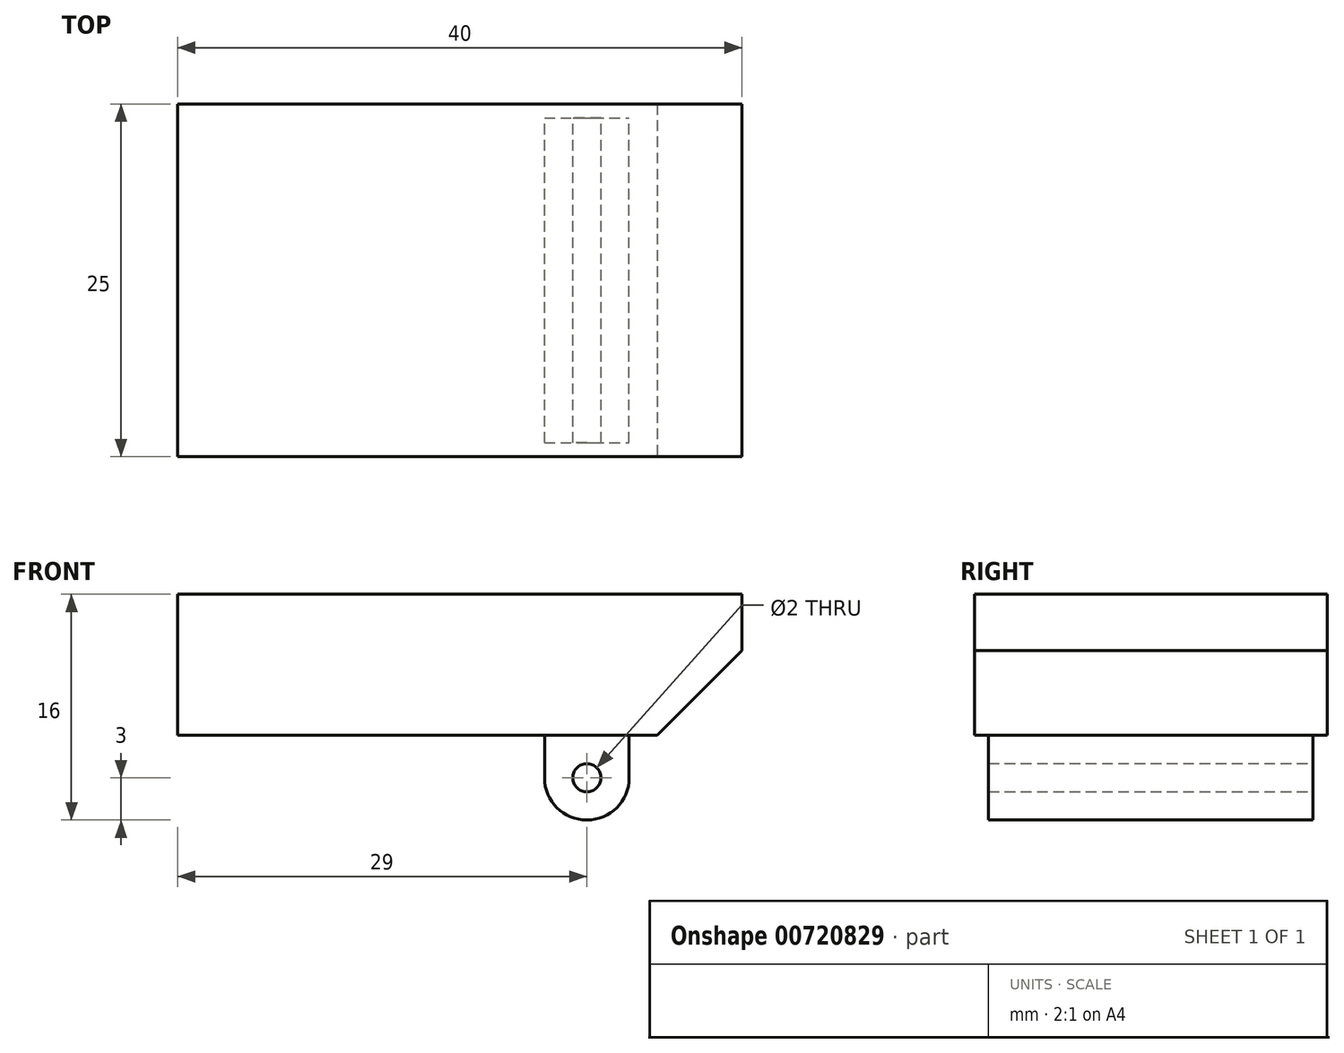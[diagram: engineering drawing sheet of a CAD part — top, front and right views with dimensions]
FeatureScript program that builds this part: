
annotation { "Feature Type Name" : "Feature", "Feature Type Description" : "" }
export const myFeature = defineFeature(function(context is Context, id is Id, definition is map)
    precondition{}
    {
        {
            var Q0;
            Q0=qCreatedBy(makeId("Top.planeOp"),FACE);
            var sketch = newSketch(context, id + "F0", { "sketchPlane" : qUnion([Q0])});
            skLineSegment(sketch, "E0.bottom", {"start": v(20, -12.5) * mm, "end": v(-20, -12.5) * mm});
            skLineSegment(sketch, "E0.top", {"start": v(20, 12.5) * mm, "end": v(-20, 12.5) * mm});
            skLineSegment(sketch, "E0.left", {"start": v(20, -12.5) * mm, "end": v(20, 12.5) * mm});
            skLineSegment(sketch, "E0.right", {"start": v(-20, -12.5) * mm, "end": v(-20, 12.5) * mm});
            skPoint(sketch, "E0.middle", {"position": v(0, 0) * mm});
            skSolve(sketch);
        }
        {
            var Q0;
            Q0=makeQuery(id+"F0.imprint","IMPRINT",FACE,{"disambiguationData":[TD([[makeQuery(id+"F0.imprint","IMPRINT",EDGE,{"derivedFrom":sQuery(id+"F0.wireOp",EDGE,"E0.bottom")}),-1.0]])]});
            extrude(context, id + "F1", {"entities" : qUnion([Q0]), "depth" : 10 * mm, "offsetDistance" : 25 * mm});
        }
        {
            var Q0;
            Q0=makeQuery(id+"F1.opExtrude","CAP_FACE",FACE,{"disambiguationData":[OSD([sQuery(id+"F0.wireOp",EDGE,"E0.bottom"),sQuery(id+"F0.wireOp",EDGE,"E0.top"),sQuery(id+"F0.wireOp",EDGE,"E0.left"),sQuery(id+"F0.wireOp",EDGE,"E0.right")])],"isStart":true});
            var sketch = newSketch(context, id + "F2", { "sketchPlane" : qUnion([Q0])});
            skLineSegment(sketch, "E1", {"start": v(20, 12.5) * mm, "end": v(12, 12.5) * mm});
            skLineSegment(sketch, "E2.bottom", {"start": v(12, 12.5) * mm, "end": v(6, 12.5) * mm});
            skLineSegment(sketch, "E2.top", {"start": v(12, -12.5) * mm, "end": v(6, -12.5) * mm});
            skLineSegment(sketch, "E2.left", {"start": v(12, 12.5) * mm, "end": v(12, -12.5) * mm});
            skLineSegment(sketch, "E2.right", {"start": v(6, 12.5) * mm, "end": v(6, -12.5) * mm});
            skSolve(sketch);
        }
        {
            var Q0;
            Q0=makeQuery(id+"F2.imprint","IMPRINT",FACE,{"disambiguationData":[TD([[makeQuery(id+"F2.imprint","IMPRINT",EDGE,{"derivedFrom":sQuery(id+"F2.wireOp",EDGE,"E2.bottom")}),1.0]])]});
            extrude(context, id + "F3", {"entities" : qUnion([Q0]), "operationType" : NewBodyOperationType.ADD, "depth" : 6 * mm, "offsetDistance" : 25 * mm});
        }
        {
            var Q0;
            Q0=makeQuery(id+"F3.opExtrude","CAP_EDGE",EDGE,{"disambiguationData":[OSD([sQuery(id+"F2.wireOp",EDGE,"E2.right")])],"isStart":false});
            var Q1;
            Q1=makeQuery(id+"F3.opExtrude","CAP_EDGE",EDGE,{"disambiguationData":[OSD([sQuery(id+"F2.wireOp",EDGE,"E2.left")])],"isStart":false});
            fillet(context, id + "F4", {"entities" : qUnion([Q0, Q1]), "radius" : 3 * mm, "tangentPropagation" : true, "allowEdgeOverflow" : false});
        }
        {
            var Q0;
            Q0=makeQuery(id+"F3.boolean.opBoolean","MERGE",FACE,{"derivedFrom":[makeQuery(id+"F1.opExtrude","SWEPT_FACE",FACE,{"disambiguationData":[OSD([sQuery(id+"F0.wireOp",EDGE,"E0.top")])]}),makeQuery(id+"F3.opExtrude","SWEPT_FACE",FACE,{"disambiguationData":[OSD([sQuery(id+"F2.wireOp",EDGE,"E2.top")])]})]});
            var sketch = newSketch(context, id + "F5", { "sketchPlane" : qUnion([Q0])});
            skCircle(sketch, "E3", {"center": v(-9, -3) * mm, "radius": 1 * mm});
            skPoint(sketch, "E4.start.orphan", {"position": v(-9, -6) * mm});
            skSolve(sketch);
        }
        {
            var Q0;
            Q0=makeQuery(id+"F5.imprint","IMPRINT",FACE,{"disambiguationData":[TD([[makeQuery(id+"F5.imprint","IMPRINT",EDGE,{"derivedFrom":sQuery(id+"F5.wireOp",EDGE,"E3")}),1.0]])]});
            extrude(context, id + "F6", {"entities" : qUnion([Q0]), "operationType" : NewBodyOperationType.REMOVE, "oppositeDirection" : true, "depth" : 30 * mm, "offsetDistance" : 25 * mm});
        }
        {
            var Q0;
            Q0=makeQuery(id+"F1.opExtrude","CAP_EDGE",EDGE,{"disambiguationData":[OSD([sQuery(id+"F0.wireOp",EDGE,"E0.left")])],"isStart":true});
            chamfer(context, id + "F7", {"entities" : qUnion([Q0]), "width" : 6 * mm, "tangentPropagation" : true});
        }
        {
            var Q0;
            Q0=makeQuery(id+"F3.boolean.opBoolean","MERGE",FACE,{"derivedFrom":[makeQuery(id+"F1.opExtrude","SWEPT_FACE",FACE,{"disambiguationData":[OSD([sQuery(id+"F0.wireOp",EDGE,"E0.top")])]}),makeQuery(id+"F3.opExtrude","SWEPT_FACE",FACE,{"disambiguationData":[OSD([sQuery(id+"F2.wireOp",EDGE,"E2.top")])]})]});
            var sketch = newSketch(context, id + "F8", { "sketchPlane" : qUnion([Q0])});
            skLineSegment(sketch, "E5", {"start": v(-6, 0) * mm, "end": v(-12, 0) * mm});
            skSolve(sketch);
        }
        {
            var Q0;
            Q0=makeQuery(id+"F8.imprint","IMPRINT",FACE,{"disambiguationData":[TD([[makeQuery(id+"F8.imprint","IMPRINT",EDGE,{"derivedFrom":sQuery(id+"F8.wireOp",EDGE,"E5")}),1.0]])]});
            extrude(context, id + "F9", {"entities" : qUnion([Q0]), "operationType" : NewBodyOperationType.REMOVE, "oppositeDirection" : true, "depth" : 1 * mm, "offsetDistance" : 25 * mm});
        }
        {
            var Q0;
            Q0=makeQuery(id+"F3.boolean.opBoolean","MERGE",FACE,{"derivedFrom":[makeQuery(id+"F1.opExtrude","SWEPT_FACE",FACE,{"disambiguationData":[OSD([sQuery(id+"F0.wireOp",EDGE,"E0.bottom")])]}),makeQuery(id+"F3.opExtrude","SWEPT_FACE",FACE,{"disambiguationData":[OSD([sQuery(id+"F2.wireOp",EDGE,"E2.bottom")])]})]});
            var sketch = newSketch(context, id + "F10", { "sketchPlane" : qUnion([Q0])});
            skLineSegment(sketch, "E6", {"start": v(6, 0) * mm, "end": v(12, 0) * mm});
            skSolve(sketch);
        }
        {
            var Q0;
            Q0=makeQuery(id+"F10.imprint","IMPRINT",FACE,{"disambiguationData":[TD([[makeQuery(id+"F10.imprint","IMPRINT",EDGE,{"derivedFrom":sQuery(id+"F10.wireOp",EDGE,"E6")}),-1.0]])]});
            extrude(context, id + "F11", {"entities" : qUnion([Q0]), "operationType" : NewBodyOperationType.REMOVE, "oppositeDirection" : true, "depth" : 1 * mm, "offsetDistance" : 25 * mm});
        }
    });
